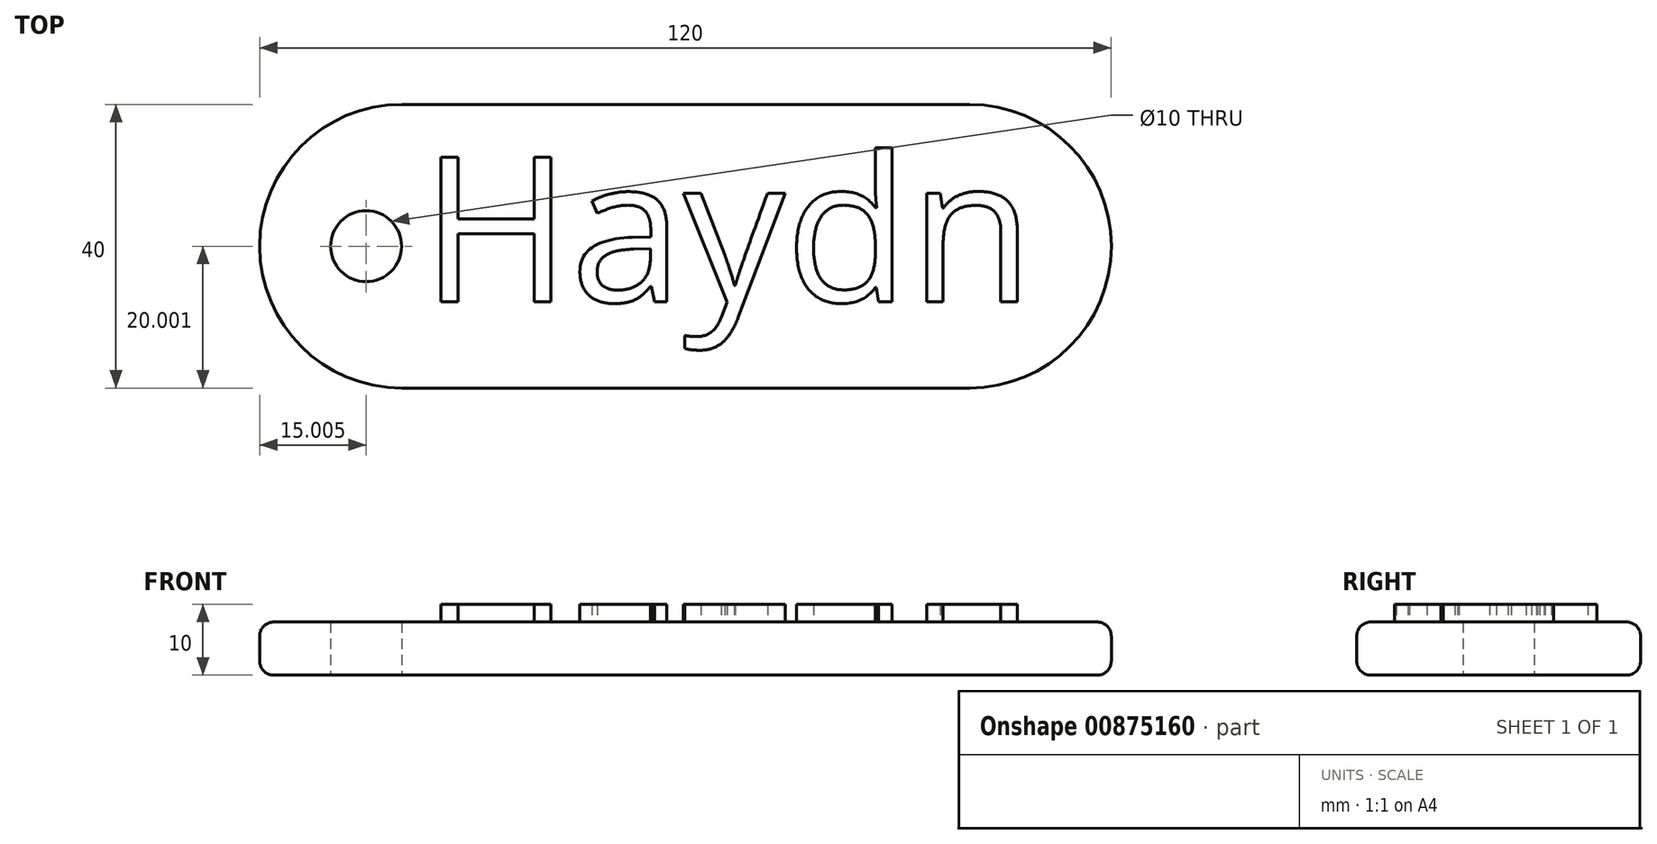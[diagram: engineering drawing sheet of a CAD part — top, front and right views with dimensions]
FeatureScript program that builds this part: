
annotation { "Feature Type Name" : "Feature", "Feature Type Description" : "" }
export const myFeature = defineFeature(function(context is Context, id is Id, definition is map)
    precondition{}
    {
        {
            var Q0;
            Q0=qCreatedBy(makeId("Top.planeOp"),FACE);
            var sketch = newSketch(context, id + "F0", { "sketchPlane" : qUnion([Q0])});
            skPoint(sketch, "E0", {"position": v(-38.02, 1.83) * mm});
            skPoint(sketch, "E1", {"position": v(41.98, 1.83) * mm});
            skPoint(sketch, "E2", {"position": v(41.98, -38.17) * mm});
            skPoint(sketch, "E3", {"position": v(-38.02, -38.17) * mm});
            skPoint(sketch, "E4", {"position": v(-58.02, -18.17) * mm});
            skPoint(sketch, "E5", {"position": v(61.98, -18.17) * mm});
            skArc(sketch, "E6", {"start": v(41.98, -38.17) * mm, "mid": v(61.98, -18.17) * mm, "end": v(41.98, 1.83) * mm});
            skLineSegment(sketch, "E7", {"start": v(-38.02, 1.83) * mm, "end": v(41.98, 1.83) * mm});
            skLineSegment(sketch, "E8", {"start": v(41.98, -38.17) * mm, "end": v(-38.02, -38.17) * mm});
            skArc(sketch, "E9", {"start": v(-38.02, 1.83) * mm, "mid": v(-58.02, -18.17) * mm, "end": v(-38.02, -38.17) * mm});
            skCircle(sketch, "E10", {"center": v(-43.02, -18.17) * mm, "radius": 5 * mm});
            skSolve(sketch);
        }
        {
            var Q0;
            Q0=makeQuery(id+"F0.imprint","IMPRINT",FACE,{"disambiguationData":[TD([[makeQuery(id+"F0.imprint","IMPRINT",EDGE,{"derivedFrom":sQuery(id+"F0.wireOp",EDGE,"E6")}),1.0]])]});
            extrude(context, id + "F1", {"entities" : qUnion([Q0]), "depth" : 7.5 * mm, "offsetDistance" : 25 * mm});
        }
        {
            var Q0;
            Q0=makeQuery(id+"F1.opExtrude","CAP_EDGE",EDGE,{"disambiguationData":[OSD([sQuery(id+"F0.wireOp",EDGE,"E7")])],"isStart":false});
            var Q1;
            Q1=makeQuery(id+"F1.opExtrude","CAP_EDGE",EDGE,{"disambiguationData":[OSD([sQuery(id+"F0.wireOp",EDGE,"E8")])],"isStart":true});
            fillet(context, id + "F2", {"entities" : qUnion([Q0, Q1]), "radius" : 2 * mm, "tangentPropagation" : true, "allowEdgeOverflow" : false});
        }
        {
            var Q0;
            Q0=makeQuery(id+"F1.opExtrude","CAP_FACE",FACE,{"disambiguationData":[OSD([sQuery(id+"F0.wireOp",EDGE,"E6"),sQuery(id+"F0.wireOp",EDGE,"E7"),sQuery(id+"F0.wireOp",EDGE,"E8"),sQuery(id+"F0.wireOp",EDGE,"E9"),sQuery(id+"F0.wireOp",EDGE,"E10")])],"isStart":false});
            var sketch = newSketch(context, id + "F3", { "sketchPlane" : qUnion([Q0])});
            skText(sketch, "E11", { "text": "Haydn", "fontName": "OpenSans-Regular.ttf"});
            const initialGuessF3  = {"E11": [-0.03525, -0.02599, 1, 0, 0.02054]};
            skSetInitialGuess(sketch, initialGuessF3);
            skSolve(sketch);
        }
        {
            var Q0;
            Q0 = qSketchRegion(id + "F3", true);
            extrude(context, id + "F4", {"entities" : qUnion([Q0]), "operationType" : NewBodyOperationType.ADD, "depth" : 2.5 * mm, "offsetDistance" : 25 * mm});
        }
    });
